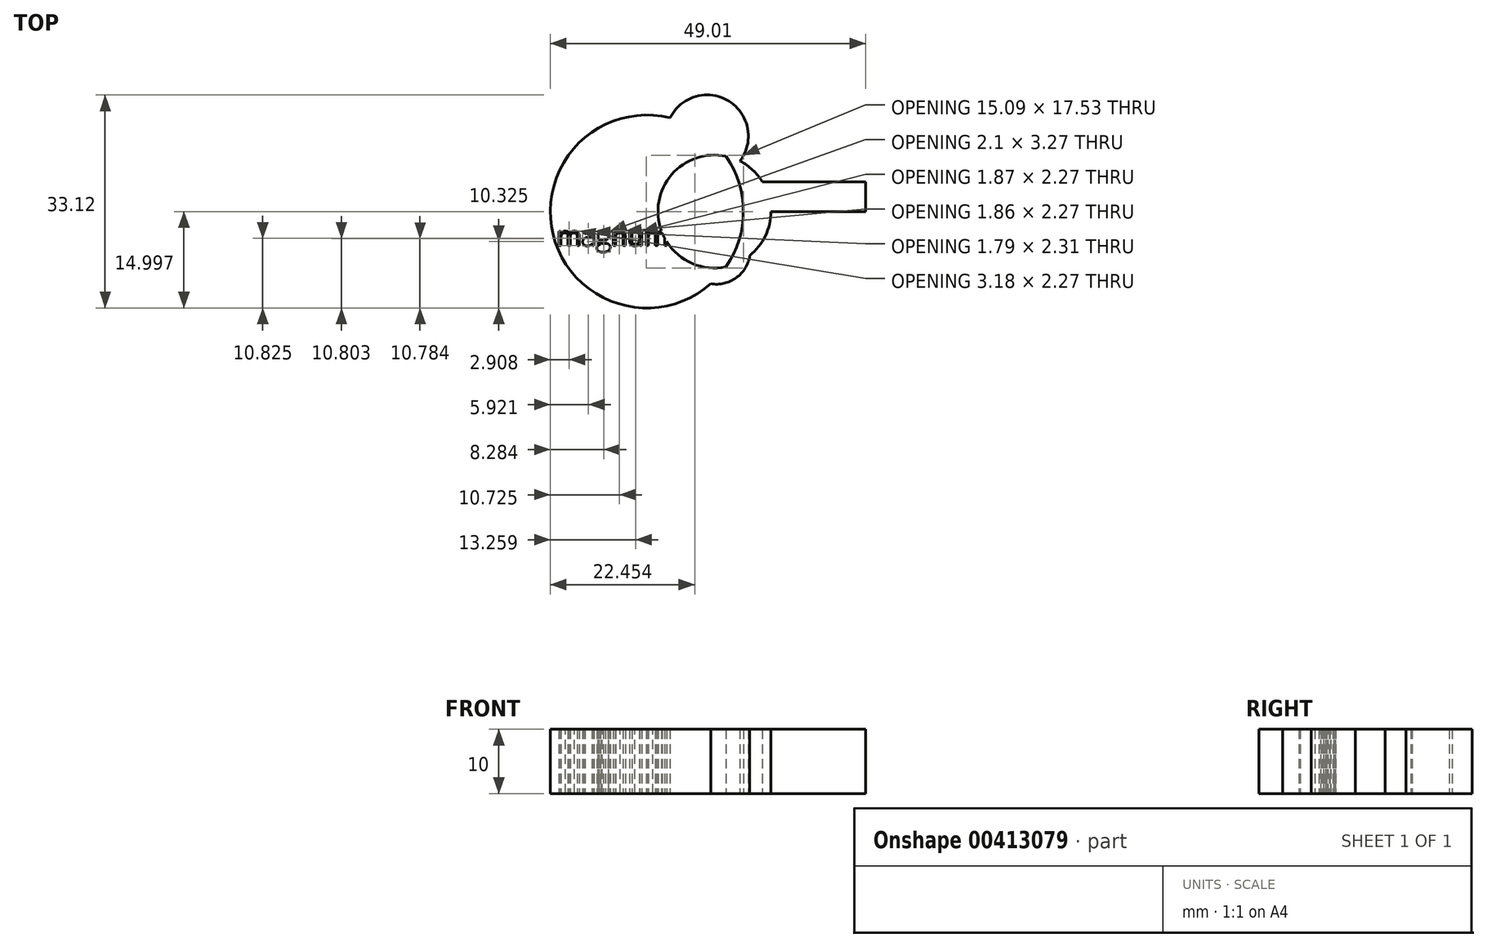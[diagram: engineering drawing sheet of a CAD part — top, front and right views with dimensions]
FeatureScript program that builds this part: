
annotation { "Feature Type Name" : "Feature", "Feature Type Description" : "" }
export const myFeature = defineFeature(function(context is Context, id is Id, definition is map)
    precondition{}
    {
        {
            var Q0;
            Q0=qCreatedBy(makeId("Top.planeOp"),FACE);
            var sketch = newSketch(context, id + "F0", { "sketchPlane" : qUnion([Q0])});
            skCircle(sketch, "E0", {"center": v(-14.95, 0) * mm, "radius": 15 * mm});
            skCircle(sketch, "E1", {"center": v(-4.44, 0) * mm, "radius": 8.78 * mm});
            skCircle(sketch, "E2", {"center": v(-5.58, 11.71) * mm, "radius": 6.41 * mm});
            skCircle(sketch, "E3", {"center": v(-4.1, -6.08) * mm, "radius": 5.22 * mm});
            skLineSegment(sketch, "E4.bottom", {"start": v(3.03, 4.62) * mm, "end": v(19.06, 4.62) * mm});
            skLineSegment(sketch, "E4.top", {"start": v(3.03, 0) * mm, "end": v(19.06, 0) * mm});
            skLineSegment(sketch, "E4.left", {"start": v(3.03, 4.62) * mm, "end": v(3.03, 0) * mm});
            skLineSegment(sketch, "E4.right", {"start": v(19.06, 4.62) * mm, "end": v(19.06, 0) * mm});
            skText(sketch, "E5", { "text": "magnum", "fontName": "OpenSans-Regular.ttf"});
            const initialGuessF0  = {"E5": [-0.02899, -0.00531, 1, 0, 0.003]};
            skSetInitialGuess(sketch, initialGuessF0);
            skSolve(sketch);
        }
        {
            var Q0;
            Q0 = qSketchRegion(id + "F0", true);
            extrude(context, id + "F1", {"entities" : qUnion([Q0]), "depth" : 10 * mm});
        }
    });
